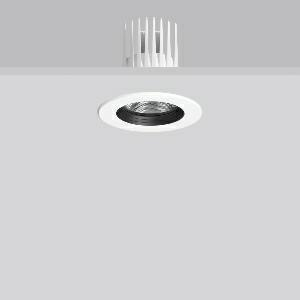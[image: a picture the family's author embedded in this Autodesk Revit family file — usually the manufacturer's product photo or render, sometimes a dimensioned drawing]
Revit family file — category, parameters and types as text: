
# Revit family: heledon_mini_e_901742_002_1_76_09af
name_source: partatom
category: Lighting Fixtures
units: mm (PartAtom-declared; Revit-internal decimal feet)

## family parameters
Cut with Voids When Loaded = No
Host = Face
Light Source = No
Part Type = Normal
Room Calculation Point = No
Round Connector Dimension = Use Diameter
Shared = No

## types (1)
- HELEDON mini E (1 x LED Modul 940, 2750 lm, 4000)
    Apparent Load = 20 VA
    Approval mark = CE
    CIE Flux Codes = 95 99 100 100 100
    Color Rendering = 92
    Color Temperature = 4000
    Default Elevation = 1800 mm
    Description = Series: HELEDON mini
Round recessed downlight. Housing: die-cast aluminium, powder-coated. Black plastic ring and recessed LED to prevent glare from the side. Optical assembly with reflector made of MIRO-Silver with 98% total light reflection for outstanding efficiency - can be changed without tools. Best colour rendering index Ra>90. Suitable for Recessed ceiling mounting. Installation without tools thanks to spring fastening system. Including separate LED converter with connecting cable 600 mm.High quality converter without flickering and stroboscopic effect. Through-wiring box (5 pole) available as accessory. The following accessories can be mounted without use of tools: interchangeable lenses, decorative glasses, honeycomb louvre, clear and frosted diffusers, white interchangeable plastic ring. 
Colour: traffic white, matt (RAL 9016)
Diameter: 124 mm
Height: 3 mm
Cut-out diameter: 114 mm
Recess height: 170 mm
Luminaire: recess height: 120 mm
Lamp: LED
Socket: without socket
Colour temperature: 4000K
Colour rendering index (CRI): 92
System power: 20 W
Rated luminous flux: 2750 lm
Luminous efficiency: 138 lm/W
Control gear: Converter, dimmable, DALI
Protection class: II
Type of protection: IP 20
    Height = 0 mm  [stored 0 ft]
    Lamp = 1 x LED Modul 940
    Lamp Light Flux = 2750 lm
    Lamp count = 1
    Length = 124 mm  [stored 0.406824 ft]
    Lifetime = 50000 h
    Luminous efficacy = 138 lm/W
    Manufacturer = RZB
    ModVariant = No
    Model = 901742.002.1.76
    Mounting Place = Ceiling
    Mounting Type = Recessed
    Number of Poles = 1
    OnlyDefault = Yes
    Power Factor = 1
    Product Name = HELEDON mini E
    Product group = Recessed downlights
    ProductGroupID = 402
    Protection Class = Protection class II
    Protection Degree = IP 20
    RLX_Detail_Level = 1
    RLX_Emergency_Light_Flux = 0 lm
    RLX_Emergency_Type = 0
    RLX_Emergency_Type_DB = No
    RlxData = <blob elided: 126197 chars, md5=5ee587af>
    Socket = socket
    Standby Power = 0 W
    System Light Flux = 2750 lm
    System Power = 20 W
    Type Comments = Product without accessories
    Type Image = 901657.002.jpg
    URL = http://relux.com
    VarID = ---
    Voltage = 230 V
    Voltage Range = 220-240 V
    Weight = 0.00 kg
    Width = 0 mm  [stored 0 ft]

note: [stored X ft] marks values corroborated as IEEE doubles in the binary element streams (Revit-internal decimal feet)

## geometry (parser evidence)
native form markers: Blend x4, Sweep x11
no freeform markers — native parametric forms only
